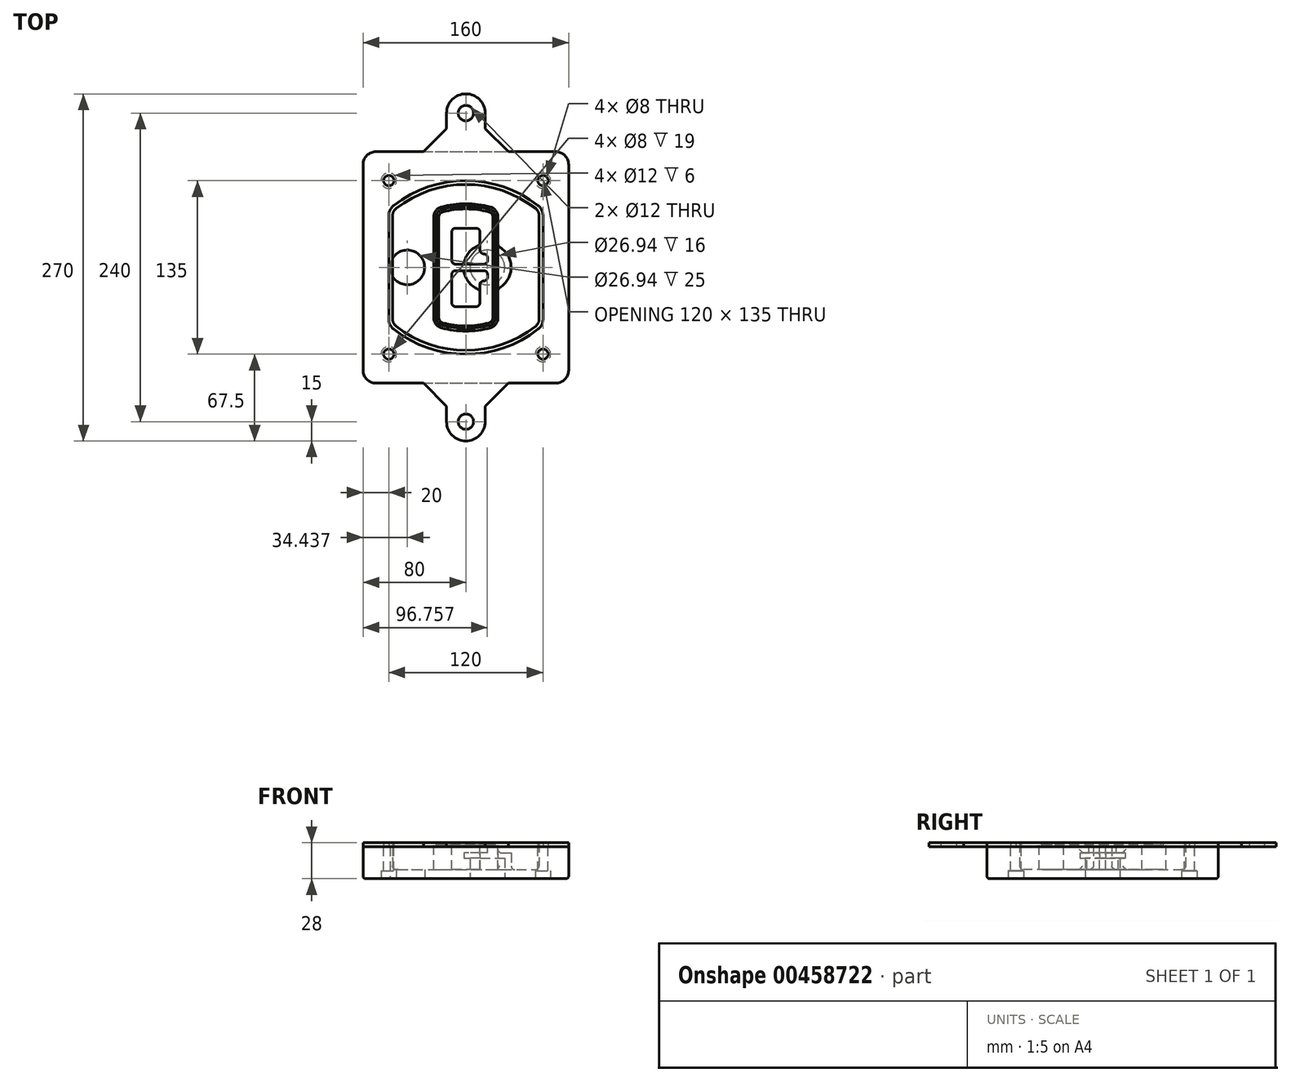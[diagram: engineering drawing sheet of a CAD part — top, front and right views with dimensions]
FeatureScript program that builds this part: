
annotation { "Feature Type Name" : "Feature", "Feature Type Description" : "" }
export const myFeature = defineFeature(function(context is Context, id is Id, definition is map)
    precondition{}
    {
        {
            var Q0;
            Q0=qCreatedBy(makeId("Top.planeOp"),FACE);
            var sketch = newSketch(context, id + "F0", { "sketchPlane" : qUnion([Q0])});
            skPoint(sketch, "E0.rect.middle", {"position": v(0, 0) * mm});
            skLineSegment(sketch, "E1.bottom", {"start": v(-70, -90) * mm, "end": v(70, -90) * mm});
            skLineSegment(sketch, "E1.top", {"start": v(-70, 90) * mm, "end": v(70, 90) * mm});
            skLineSegment(sketch, "E1.left", {"start": v(-80, -80) * mm, "end": v(-80, 80) * mm});
            skLineSegment(sketch, "E1.right", {"start": v(80, -80) * mm, "end": v(80, 80) * mm});
            skLineSegment(sketch, "E2", {"start": v(-80, 90) * mm, "end": v(80, -90) * mm, "construction": true});
            skLineSegment(sketch, "E3", {"start": v(80, 90) * mm, "end": v(-80, -90) * mm, "construction": true});
            skCircle(sketch, "E4", {"center": v(-60, 67.5) * mm, "radius": 4 * mm});
            skCircle(sketch, "E5", {"center": v(60, 67.5) * mm, "radius": 4 * mm});
            skCircle(sketch, "E6", {"center": v(60, -67.5) * mm, "radius": 4 * mm});
            skCircle(sketch, "E7", {"center": v(-60, -67.5) * mm, "radius": 4 * mm});
            skLineSegment(sketch, "E8", {"start": v(-60, 67.5) * mm, "end": v(60, 67.5) * mm, "construction": true});
            skLineSegment(sketch, "E9", {"start": v(60, 67.5) * mm, "end": v(60, -67.5) * mm, "construction": true});
            skLineSegment(sketch, "E10", {"start": v(60, -67.5) * mm, "end": v(-60, -67.5) * mm, "construction": true});
            skLineSegment(sketch, "E11", {"start": v(-60, -67.5) * mm, "end": v(-60, 67.5) * mm, "construction": true});
            skLineSegment(sketch, "E12", {"start": v(-60, 40.3) * mm, "end": v(-60, -40.3) * mm});
            skLineSegment(sketch, "E13", {"start": v(60, 40.3) * mm, "end": v(60, -40.3) * mm});
            skArc(sketch, "E14", {"start": v(56.15, 48.18) * mm, "mid": v(0, 67.5) * mm, "end": v(-56.15, 48.18) * mm});
            skArc(sketch, "E15", {"start": v(-56.15, -48.18) * mm, "mid": v(0, -67.5) * mm, "end": v(56.15, -48.18) * mm});
            skLineSegment(sketch, "E16", {"start": v(-60, 0) * mm, "end": v(60, 0) * mm, "construction": true});
            skPoint(sketch, "E17.visualSharp", {"position": v(-60, -45) * mm});
            skArc(sketch, "E17.filletArc", {"start": v(-60, -40.3) * mm, "mid": v(-58.99, -44.68) * mm, "end": v(-56.15, -48.18) * mm});
            skPoint(sketch, "E18.visualSharp", {"position": v(-60, 45) * mm});
            skArc(sketch, "E18.filletArc", {"start": v(-56.15, 48.18) * mm, "mid": v(-58.99, 44.68) * mm, "end": v(-60, 40.3) * mm});
            skPoint(sketch, "E19.visualSharp", {"position": v(60, 45) * mm});
            skArc(sketch, "E19.filletArc", {"start": v(60, 40.3) * mm, "mid": v(58.99, 44.68) * mm, "end": v(56.15, 48.18) * mm});
            skPoint(sketch, "E20.visualSharp", {"position": v(60, -45) * mm});
            skArc(sketch, "E20.filletArc", {"start": v(56.15, -48.18) * mm, "mid": v(58.99, -44.68) * mm, "end": v(60, -40.3) * mm});
            skPoint(sketch, "E21.visualSharp", {"position": v(-80, 90) * mm});
            skArc(sketch, "E21.filletArc", {"start": v(-70, 90) * mm, "mid": v(-77.07, 87.07) * mm, "end": v(-80, 80) * mm});
            skPoint(sketch, "E22.visualSharp", {"position": v(80, 90) * mm});
            skArc(sketch, "E22.filletArc", {"start": v(80, 80) * mm, "mid": v(77.07, 87.07) * mm, "end": v(70, 90) * mm});
            skPoint(sketch, "E23.visualSharp", {"position": v(80, -90) * mm});
            skArc(sketch, "E23.filletArc", {"start": v(70, -90) * mm, "mid": v(77.07, -87.07) * mm, "end": v(80, -80) * mm});
            skPoint(sketch, "E24.visualSharp", {"position": v(-80, -90) * mm});
            skArc(sketch, "E24.filletArc", {"start": v(-80, -80) * mm, "mid": v(-77.07, -87.07) * mm, "end": v(-70, -90) * mm});
            skArc(sketch, "E25.0", {"start": v(57, 40.3) * mm, "mid": v(56.3, 43.36) * mm, "end": v(54.3, 45.81) * mm});
            skLineSegment(sketch, "E25.1", {"start": v(57, 40.3) * mm, "end": v(57, -40.3) * mm});
            skArc(sketch, "E25.2", {"start": v(54.3, -45.81) * mm, "mid": v(56.3, -43.36) * mm, "end": v(57, -40.3) * mm});
            skArc(sketch, "E25.3", {"start": v(-54.3, -45.81) * mm, "mid": v(0, -64.5) * mm, "end": v(54.3, -45.81) * mm});
            skArc(sketch, "E25.4", {"start": v(-57, -40.3) * mm, "mid": v(-56.3, -43.36) * mm, "end": v(-54.3, -45.81) * mm});
            skArc(sketch, "E25.5", {"start": v(54.3, 45.81) * mm, "mid": v(0, 64.5) * mm, "end": v(-54.3, 45.81) * mm});
            skLineSegment(sketch, "E25.6", {"start": v(-57, 40.3) * mm, "end": v(-57, -40.3) * mm});
            skArc(sketch, "E25.7", {"start": v(-54.3, 45.81) * mm, "mid": v(-56.3, 43.36) * mm, "end": v(-57, 40.3) * mm});
            skArc(sketch, "E26.0", {"start": v(-58.62, 51.33) * mm, "mid": v(-62.58, 46.43) * mm, "end": v(-64, 40.3) * mm});
            skArc(sketch, "E26.1", {"start": v(58.62, 51.33) * mm, "mid": v(0, 71.5) * mm, "end": v(-58.62, 51.33) * mm});
            skArc(sketch, "E26.2", {"start": v(64, 40.3) * mm, "mid": v(62.58, 46.43) * mm, "end": v(58.62, 51.33) * mm});
            skLineSegment(sketch, "E26.3", {"start": v(64, 40.3) * mm, "end": v(64, -40.3) * mm});
            skArc(sketch, "E26.4", {"start": v(58.62, -51.33) * mm, "mid": v(62.58, -46.43) * mm, "end": v(64, -40.3) * mm});
            skLineSegment(sketch, "E26.5", {"start": v(-64, 40.3) * mm, "end": v(-64, -40.3) * mm});
            skArc(sketch, "E26.6", {"start": v(-58.62, -51.33) * mm, "mid": v(0, -71.5) * mm, "end": v(58.62, -51.33) * mm});
            skArc(sketch, "E26.7", {"start": v(-64, -40.3) * mm, "mid": v(-62.58, -46.43) * mm, "end": v(-58.62, -51.33) * mm});
            skSolve(sketch);
        }
        {
            var Q0;
            Q0=makeQuery(id+"F0.imprint","IMPRINT",FACE,{"disambiguationData":[TD([[makeQuery(id+"F0.imprint","IMPRINT",EDGE,{"derivedFrom":sQuery(id+"F0.wireOp",EDGE,"E1.bottom")}),1.0]])]});
            var Q1;
            Q1=makeQuery(id+"F0.imprint","IMPRINT",FACE,{"disambiguationData":[TD([[makeQuery(id+"F0.imprint","IMPRINT",EDGE,{"derivedFrom":sQuery(id+"F0.wireOp",EDGE,"E12")}),1.0]])]});
            var Q2;
            Q2=makeQuery(id+"F0.imprint","IMPRINT",FACE,{"disambiguationData":[TD([[makeQuery(id+"F0.imprint","IMPRINT",EDGE,{"derivedFrom":sQuery(id+"F0.wireOp",EDGE,"E25.0")}),1.0]])]});
            var Q3;
            Q3=makeQuery(id+"F0.imprint","IMPRINT",FACE,{"disambiguationData":[TD([[makeQuery(id+"F0.imprint","IMPRINT",EDGE,{"derivedFrom":sQuery(id+"F0.wireOp",EDGE,"E12")}),-1.0]])]});
            extrude(context, id + "F1", {"entities" : qUnion([Q0, Q1, Q2, Q3]), "oppositeDirection" : true, "depth" : 25 * mm});
        }
        {
            var Q0;
            Q0=makeQuery(id+"F0.imprint","IMPRINT",FACE,{"disambiguationData":[TD([[makeQuery(id+"F0.imprint","IMPRINT",EDGE,{"derivedFrom":sQuery(id+"F0.wireOp",EDGE,"E12")}),1.0]])]});
            extrude(context, id + "F2", {"entities" : qUnion([Q0]), "operationType" : NewBodyOperationType.ADD, "depth" : 3 * mm});
        }
        {
            var Q0;
            Q0=makeQuery(id+"F0.imprint","IMPRINT",FACE,{"disambiguationData":[TD([[makeQuery(id+"F0.imprint","IMPRINT",EDGE,{"derivedFrom":sQuery(id+"F0.wireOp",EDGE,"E25.0")}),1.0]])]});
            extrude(context, id + "F3", {"entities" : qUnion([Q0]), "operationType" : NewBodyOperationType.REMOVE, "oppositeDirection" : true, "depth" : 18 * mm});
        }
        {
            var Q0;
            Q0=makeQuery(id+"F2.opExtrude","CAP_FACE",FACE,{"disambiguationData":[OSD([sQuery(id+"F0.wireOp",EDGE,"E12"),sQuery(id+"F0.wireOp",EDGE,"E13"),sQuery(id+"F0.wireOp",EDGE,"E14"),sQuery(id+"F0.wireOp",EDGE,"E15"),sQuery(id+"F0.wireOp",EDGE,"E17.filletArc"),sQuery(id+"F0.wireOp",EDGE,"E18.filletArc"),sQuery(id+"F0.wireOp",EDGE,"E19.filletArc"),sQuery(id+"F0.wireOp",EDGE,"E20.filletArc"),sQuery(id+"F0.wireOp",EDGE,"E25.0"),sQuery(id+"F0.wireOp",EDGE,"E25.1"),sQuery(id+"F0.wireOp",EDGE,"E25.2"),sQuery(id+"F0.wireOp",EDGE,"E25.3"),sQuery(id+"F0.wireOp",EDGE,"E25.4"),sQuery(id+"F0.wireOp",EDGE,"E25.5"),sQuery(id+"F0.wireOp",EDGE,"E25.6"),sQuery(id+"F0.wireOp",EDGE,"E25.7")])],"isStart":false});
            var sketch = newSketch(context, id + "F4", { "sketchPlane" : qUnion([Q0])});
            skArc(sketch, "E27.0", {"start": v(-19.08, -46.97) * mm, "mid": v(0, -49.5) * mm, "end": v(19.08, -46.97) * mm});
            skArc(sketch, "E28.0", {"start": v(19.08, 46.97) * mm, "mid": v(0, 49.5) * mm, "end": v(-19.08, 46.97) * mm});
            skLineSegment(sketch, "E29", {"start": v(-25, 39.25) * mm, "end": v(-25, -39.25) * mm});
            skLineSegment(sketch, "E30", {"start": v(25, 39.25) * mm, "end": v(25, -39.25) * mm});
            skLineSegment(sketch, "E31", {"start": v(-25, 45.1) * mm, "end": v(25, 45.1) * mm, "construction": true});
            skLineSegment(sketch, "E32", {"start": v(-25, -45.1) * mm, "end": v(25, -45.1) * mm, "construction": true});
            skPoint(sketch, "E33.visualSharp", {"position": v(-25, 45.1) * mm});
            skArc(sketch, "E33.filletArc", {"start": v(-19.08, 46.97) * mm, "mid": v(-23.35, 44.11) * mm, "end": v(-25, 39.25) * mm});
            skPoint(sketch, "E34.visualSharp", {"position": v(25, 45.1) * mm});
            skArc(sketch, "E34.filletArc", {"start": v(25, 39.25) * mm, "mid": v(23.35, 44.11) * mm, "end": v(19.08, 46.97) * mm});
            skPoint(sketch, "E35.visualSharp", {"position": v(25, -45.1) * mm});
            skArc(sketch, "E35.filletArc", {"start": v(19.08, -46.97) * mm, "mid": v(23.35, -44.11) * mm, "end": v(25, -39.25) * mm});
            skPoint(sketch, "E36.visualSharp", {"position": v(-25, -45.1) * mm});
            skArc(sketch, "E36.filletArc", {"start": v(-25, -39.25) * mm, "mid": v(-23.35, -44.11) * mm, "end": v(-19.08, -46.97) * mm});
            skArc(sketch, "E37.0", {"start": v(54.3, 45.81) * mm, "mid": v(0, 64.5) * mm, "end": v(-54.3, 45.81) * mm});
            skArc(sketch, "E37.1", {"start": v(-54.3, 45.81) * mm, "mid": v(-56.3, 43.36) * mm, "end": v(-57, 40.3) * mm});
            skLineSegment(sketch, "E37.2", {"start": v(-57, 40.3) * mm, "end": v(-57, -40.3) * mm});
            skArc(sketch, "E37.3", {"start": v(-57, -40.3) * mm, "mid": v(-56.3, -43.36) * mm, "end": v(-54.3, -45.81) * mm});
            skArc(sketch, "E37.4", {"start": v(-54.3, -45.81) * mm, "mid": v(0, -64.5) * mm, "end": v(54.3, -45.81) * mm});
            skArc(sketch, "E37.5", {"start": v(54.3, -45.81) * mm, "mid": v(56.3, -43.36) * mm, "end": v(57, -40.3) * mm});
            skLineSegment(sketch, "E37.6", {"start": v(57, 40.3) * mm, "end": v(57, -40.3) * mm});
            skArc(sketch, "E37.7", {"start": v(57, 40.3) * mm, "mid": v(56.3, 43.36) * mm, "end": v(54.3, 45.81) * mm});
            skLineSegment(sketch, "E38.0", {"start": v(23, 39.25) * mm, "end": v(23, -39.25) * mm});
            skArc(sketch, "E38.1", {"start": v(18.56, -45.04) * mm, "mid": v(21.76, -42.9) * mm, "end": v(23, -39.25) * mm});
            skArc(sketch, "E38.2", {"start": v(-18.56, -45.04) * mm, "mid": v(0, -47.5) * mm, "end": v(18.56, -45.04) * mm});
            skArc(sketch, "E38.3", {"start": v(-23, -39.25) * mm, "mid": v(-21.76, -42.9) * mm, "end": v(-18.56, -45.04) * mm});
            skLineSegment(sketch, "E38.4", {"start": v(-23, 39.25) * mm, "end": v(-23, -39.25) * mm});
            skArc(sketch, "E38.5", {"start": v(23, 39.25) * mm, "mid": v(21.76, 42.9) * mm, "end": v(18.56, 45.04) * mm});
            skArc(sketch, "E38.6", {"start": v(-18.56, 45.04) * mm, "mid": v(-21.76, 42.9) * mm, "end": v(-23, 39.25) * mm});
            skArc(sketch, "E38.7", {"start": v(18.56, 45.04) * mm, "mid": v(0, 47.5) * mm, "end": v(-18.56, 45.04) * mm});
            skArc(sketch, "E39.0", {"start": v(21, 39.25) * mm, "mid": v(20.18, 41.68) * mm, "end": v(18.04, 43.1) * mm});
            skLineSegment(sketch, "E39.1", {"start": v(21, 39.25) * mm, "end": v(21, -39.25) * mm});
            skArc(sketch, "E39.2", {"start": v(18.04, -43.1) * mm, "mid": v(20.18, -41.68) * mm, "end": v(21, -39.25) * mm});
            skArc(sketch, "E39.3", {"start": v(-18.04, -43.1) * mm, "mid": v(0, -45.5) * mm, "end": v(18.04, -43.1) * mm});
            skArc(sketch, "E39.4", {"start": v(-21, -39.25) * mm, "mid": v(-20.18, -41.68) * mm, "end": v(-18.04, -43.1) * mm});
            skArc(sketch, "E39.5", {"start": v(18.04, 43.1) * mm, "mid": v(0, 45.5) * mm, "end": v(-18.04, 43.1) * mm});
            skLineSegment(sketch, "E39.6", {"start": v(-21, 39.25) * mm, "end": v(-21, -39.25) * mm});
            skArc(sketch, "E39.7", {"start": v(-18.04, 43.1) * mm, "mid": v(-20.18, 41.68) * mm, "end": v(-21, 39.25) * mm});
            skLineSegment(sketch, "E40", {"start": v(-25, 0) * mm, "end": v(25, 0) * mm, "construction": true});
            skLineSegment(sketch, "E41", {"start": v(-11, 5.5) * mm, "end": v(-11, 27.5) * mm});
            skLineSegment(sketch, "E42", {"start": v(-8, 30.5) * mm, "end": v(8, 30.5) * mm});
            skLineSegment(sketch, "E43", {"start": v(11, 27.5) * mm, "end": v(11, 13.5) * mm});
            skLineSegment(sketch, "E44", {"start": v(14, 10.5) * mm, "end": v(14, 10.5) * mm});
            skLineSegment(sketch, "E45", {"start": v(17, 7.5) * mm, "end": v(17, 5.5) * mm});
            skLineSegment(sketch, "E46", {"start": v(14, 2.5) * mm, "end": v(-8, 2.5) * mm});
            skPoint(sketch, "E47.visualSharp", {"position": v(-11, 30.5) * mm});
            skArc(sketch, "E47.filletArc", {"start": v(-8, 30.5) * mm, "mid": v(-10.12, 29.62) * mm, "end": v(-11, 27.5) * mm});
            skPoint(sketch, "E48.visualSharp", {"position": v(11, 30.5) * mm});
            skArc(sketch, "E48.filletArc", {"start": v(11, 27.5) * mm, "mid": v(10.12, 29.62) * mm, "end": v(8, 30.5) * mm});
            skPoint(sketch, "E49.visualSharp", {"position": v(11, 10.5) * mm});
            skArc(sketch, "E49.filletArc", {"start": v(11, 13.5) * mm, "mid": v(11.88, 11.38) * mm, "end": v(14, 10.5) * mm});
            skPoint(sketch, "E50.visualSharp", {"position": v(17, 10.5) * mm});
            skArc(sketch, "E50.filletArc", {"start": v(17, 7.5) * mm, "mid": v(16.12, 9.62) * mm, "end": v(14, 10.5) * mm});
            skPoint(sketch, "E51.visualSharp", {"position": v(17, 2.5) * mm});
            skArc(sketch, "E51.filletArc", {"start": v(14, 2.5) * mm, "mid": v(16.12, 3.38) * mm, "end": v(17, 5.5) * mm});
            skPoint(sketch, "E52.visualSharp", {"position": v(-11, 2.5) * mm});
            skArc(sketch, "E52.filletArc", {"start": v(-11, 5.5) * mm, "mid": v(-10.12, 3.38) * mm, "end": v(-8, 2.5) * mm});
            skLineSegment(sketch, "E53.0.MirrorCS", {"start": v(14, -2.5) * mm, "end": v(-8, -2.5) * mm});
            skArc(sketch, "E54.0.MirrorCS", {"start": v(-11, -5.5) * mm, "mid": v(-10.12, -3.38) * mm, "end": v(-8, -2.5) * mm});
            skLineSegment(sketch, "E55.0.MirrorCS", {"start": v(-11, -5.5) * mm, "end": v(-11, -27.5) * mm});
            skArc(sketch, "E56.0.MirrorCS", {"start": v(-8, -30.5) * mm, "mid": v(-10.12, -29.62) * mm, "end": v(-11, -27.5) * mm});
            skLineSegment(sketch, "E57.0.MirrorCS", {"start": v(-8, -30.5) * mm, "end": v(8, -30.5) * mm});
            skArc(sketch, "E58.0.MirrorCS", {"start": v(11, -27.5) * mm, "mid": v(10.12, -29.62) * mm, "end": v(8, -30.5) * mm});
            skLineSegment(sketch, "E59.0.MirrorCS", {"start": v(11, -27.5) * mm, "end": v(11, -13.5) * mm});
            skArc(sketch, "E60.0.MirrorCS", {"start": v(11, -13.5) * mm, "mid": v(11.88, -11.38) * mm, "end": v(14, -10.5) * mm});
            skArc(sketch, "E61.0.MirrorCS", {"start": v(17, -7.5) * mm, "mid": v(16.12, -9.62) * mm, "end": v(14, -10.5) * mm});
            skLineSegment(sketch, "E62.0.MirrorCS", {"start": v(17, -7.5) * mm, "end": v(17, -5.5) * mm});
            skArc(sketch, "E63.0.MirrorCS", {"start": v(14, -2.5) * mm, "mid": v(16.12, -3.38) * mm, "end": v(17, -5.5) * mm});
            skSolve(sketch);
        }
        {
            var Q0;
            Q0=makeQuery(id+"F4.imprint","IMPRINT",FACE,{"disambiguationData":[TD([[makeQuery(id+"F4.imprint","IMPRINT",EDGE,{"derivedFrom":sQuery(id+"F4.wireOp",EDGE,"E27.0")}),1.0]])]});
            var Q1;
            Q1=makeQuery(id+"F4.imprint","IMPRINT",FACE,{"disambiguationData":[TD([[makeQuery(id+"F4.imprint","IMPRINT",EDGE,{"derivedFrom":sQuery(id+"F4.wireOp",EDGE,"E38.0")}),-1.0]])]});
            var Q2;
            Q2=makeQuery(id+"F4.imprint","IMPRINT",FACE,{"disambiguationData":[TD([[makeQuery(id+"F4.imprint","IMPRINT",EDGE,{"derivedFrom":sQuery(id+"F4.wireOp",EDGE,"E39.0")}),1.0]])]});
            extrude(context, id + "F5", {"entities" : qUnion([Q0, Q1, Q2]), "operationType" : NewBodyOperationType.ADD, "endBound" : BoundingType.UP_TO_NEXT, "oppositeDirection" : true, "depth" : 25 * mm});
        }
        {
            var Q0;
            Q0=makeQuery(id+"F4.imprint","IMPRINT",FACE,{"disambiguationData":[TD([[makeQuery(id+"F4.imprint","IMPRINT",EDGE,{"derivedFrom":sQuery(id+"F4.wireOp",EDGE,"E38.0")}),-1.0]])]});
            extrude(context, id + "F6", {"entities" : qUnion([Q0]), "operationType" : NewBodyOperationType.REMOVE, "oppositeDirection" : true, "depth" : 2 * mm});
        }
        {
            var Q0;
            Q0=makeQuery(id+"F1.opExtrude","CAP_FACE",FACE,{"disambiguationData":[OSD([sQuery(id+"F0.wireOp",EDGE,"E1.bottom"),sQuery(id+"F0.wireOp",EDGE,"E1.top"),sQuery(id+"F0.wireOp",EDGE,"E1.left"),sQuery(id+"F0.wireOp",EDGE,"E1.right"),sQuery(id+"F0.wireOp",EDGE,"E4"),sQuery(id+"F0.wireOp",EDGE,"E5"),sQuery(id+"F0.wireOp",EDGE,"E6"),sQuery(id+"F0.wireOp",EDGE,"E7"),sQuery(id+"F0.wireOp",EDGE,"E21.filletArc"),sQuery(id+"F0.wireOp",EDGE,"E22.filletArc"),sQuery(id+"F0.wireOp",EDGE,"E23.filletArc"),sQuery(id+"F0.wireOp",EDGE,"E24.filletArc")])],"isStart":false});
            var sketch = newSketch(context, id + "F7", { "sketchPlane" : qUnion([Q0])});
            skCircle(sketch, "E64", {"center": v(16.76, 0) * mm, "radius": 13.47 * mm});
            skCircle(sketch, "E65", {"center": v(-45.56, 0) * mm, "radius": 13.47 * mm});
            skLineSegment(sketch, "E66", {"start": v(80, 0) * mm, "end": v(-80, 0) * mm});
            skCircle(sketch, "E67", {"center": v(16.76, 0) * mm, "radius": 18.47 * mm});
            skCircle(sketch, "E68", {"center": v(60, -67.5) * mm, "radius": 6 * mm});
            skCircle(sketch, "E69", {"center": v(-60, -67.5) * mm, "radius": 6 * mm});
            skCircle(sketch, "E70", {"center": v(-60, 67.5) * mm, "radius": 6 * mm});
            skCircle(sketch, "E71", {"center": v(60, 67.5) * mm, "radius": 6 * mm});
            skSolve(sketch);
        }
        {
            var Q0;
            {var subQ1=sQuery(id+"F7.wireOp",EDGE,"E66");var subQ4=sQuery(id+"F7.wireOp",EDGE,"E64");var subQ6=makeQuery(id+"F7.imprint","INTERSECT",VERTEX,{"disambiguationData":[OD(0.0)],"derivedFrom":[subQ4,subQ1]});Q0=makeQuery(id+"F7.imprint","IMPRINT",FACE,{"disambiguationData":[TD([[makeQuery(id+"F7.imprint","IMPRINT",EDGE,{"disambiguationData":[TD([[subQ6,-1.0]])],"derivedFrom":subQ4}),-1.0]])]});}
            var Q1;
            {var subQ0=sQuery(id+"F7.wireOp",EDGE,"E66");var subQ1=sQuery(id+"F7.wireOp",EDGE,"E64");var subQ3=makeQuery(id+"F7.imprint","INTERSECT",VERTEX,{"disambiguationData":[OD(0.0)],"derivedFrom":[subQ1,subQ0]});Q1=makeQuery(id+"F7.imprint","IMPRINT",FACE,{"disambiguationData":[TD([[makeQuery(id+"F7.imprint","IMPRINT",EDGE,{"disambiguationData":[TD([[subQ3,-1.0]])],"derivedFrom":subQ1}),1.0]])]});}
            var Q2;
            {var subQ0=sQuery(id+"F7.wireOp",EDGE,"E66");var subQ1=sQuery(id+"F7.wireOp",EDGE,"E64");var subQ3=makeQuery(id+"F7.imprint","INTERSECT",VERTEX,{"disambiguationData":[OD(0.0)],"derivedFrom":[subQ1,subQ0]});Q2=makeQuery(id+"F7.imprint","IMPRINT",FACE,{"disambiguationData":[TD([[makeQuery(id+"F7.imprint","IMPRINT",EDGE,{"disambiguationData":[TD([[subQ3,1.0]])],"derivedFrom":subQ1}),1.0]])]});}
            var Q3;
            {var subQ1=sQuery(id+"F7.wireOp",EDGE,"E66");var subQ4=sQuery(id+"F7.wireOp",EDGE,"E64");var subQ6=makeQuery(id+"F7.imprint","INTERSECT",VERTEX,{"disambiguationData":[OD(0.0)],"derivedFrom":[subQ4,subQ1]});Q3=makeQuery(id+"F7.imprint","IMPRINT",FACE,{"disambiguationData":[TD([[makeQuery(id+"F7.imprint","IMPRINT",EDGE,{"disambiguationData":[TD([[subQ6,1.0]])],"derivedFrom":subQ4}),-1.0]])]});}
            extrude(context, id + "F8", {"entities" : qUnion([Q0, Q1, Q2, Q3]), "operationType" : NewBodyOperationType.ADD, "oppositeDirection" : true, "depth" : 20 * mm});
        }
        {
            var Q0;
            {var subQ0=sQuery(id+"F7.wireOp",EDGE,"E66");var subQ1=sQuery(id+"F7.wireOp",EDGE,"E64");var subQ3=makeQuery(id+"F7.imprint","INTERSECT",VERTEX,{"disambiguationData":[OD(0.0)],"derivedFrom":[subQ1,subQ0]});Q0=makeQuery(id+"F7.imprint","IMPRINT",FACE,{"disambiguationData":[TD([[makeQuery(id+"F7.imprint","IMPRINT",EDGE,{"disambiguationData":[TD([[subQ3,-1.0]])],"derivedFrom":subQ1}),1.0]])]});}
            var Q1;
            {var subQ0=sQuery(id+"F7.wireOp",EDGE,"E66");var subQ1=sQuery(id+"F7.wireOp",EDGE,"E64");var subQ3=makeQuery(id+"F7.imprint","INTERSECT",VERTEX,{"disambiguationData":[OD(0.0)],"derivedFrom":[subQ1,subQ0]});Q1=makeQuery(id+"F7.imprint","IMPRINT",FACE,{"disambiguationData":[TD([[makeQuery(id+"F7.imprint","IMPRINT",EDGE,{"disambiguationData":[TD([[subQ3,1.0]])],"derivedFrom":subQ1}),1.0]])]});}
            extrude(context, id + "F9", {"entities" : qUnion([Q0, Q1]), "operationType" : NewBodyOperationType.REMOVE, "oppositeDirection" : true, "depth" : 16 * mm});
        }
        {
            var Q0;
            {var subQ0=sQuery(id+"F7.wireOp",EDGE,"E66");var subQ1=sQuery(id+"F7.wireOp",EDGE,"E65");var subQ3=makeQuery(id+"F7.imprint","INTERSECT",VERTEX,{"disambiguationData":[OD(0.0)],"derivedFrom":[subQ1,subQ0]});Q0=makeQuery(id+"F7.imprint","IMPRINT",FACE,{"disambiguationData":[TD([[makeQuery(id+"F7.imprint","IMPRINT",EDGE,{"disambiguationData":[TD([[subQ3,-1.0]])],"derivedFrom":subQ1}),1.0]])]});}
            var Q1;
            {var subQ0=sQuery(id+"F7.wireOp",EDGE,"E66");var subQ1=sQuery(id+"F7.wireOp",EDGE,"E65");var subQ3=makeQuery(id+"F7.imprint","INTERSECT",VERTEX,{"disambiguationData":[OD(0.0)],"derivedFrom":[subQ1,subQ0]});Q1=makeQuery(id+"F7.imprint","IMPRINT",FACE,{"disambiguationData":[TD([[makeQuery(id+"F7.imprint","IMPRINT",EDGE,{"disambiguationData":[TD([[subQ3,1.0]])],"derivedFrom":subQ1}),1.0]])]});}
            extrude(context, id + "F10", {"entities" : qUnion([Q0, Q1]), "operationType" : NewBodyOperationType.REMOVE, "oppositeDirection" : true, "depth" : 25 * mm});
        }
        {
            var Q0;
            Q0=makeQuery(id+"F7.imprint","IMPRINT",FACE,{"disambiguationData":[TD([[makeQuery(id+"F7.imprint","IMPRINT",EDGE,{"derivedFrom":sQuery(id+"F7.wireOp",EDGE,"E68")}),1.0]])]});
            var Q1;
            Q1=makeQuery(id+"F7.imprint","IMPRINT",FACE,{"disambiguationData":[TD([[makeQuery(id+"F7.imprint","IMPRINT",EDGE,{"derivedFrom":makeQuery(id+"F1.opExtrude","CAP_EDGE",EDGE,{"disambiguationData":[OSD([sQuery(id+"F0.wireOp",EDGE,"E5")])],"isStart":false})}),-1.0]])]});
            var Q2;
            Q2=makeQuery(id+"F7.imprint","IMPRINT",FACE,{"disambiguationData":[TD([[makeQuery(id+"F7.imprint","IMPRINT",EDGE,{"derivedFrom":sQuery(id+"F7.wireOp",EDGE,"E69")}),1.0]])]});
            var Q3;
            Q3=makeQuery(id+"F7.imprint","IMPRINT",FACE,{"disambiguationData":[TD([[makeQuery(id+"F7.imprint","IMPRINT",EDGE,{"derivedFrom":makeQuery(id+"F1.opExtrude","CAP_EDGE",EDGE,{"disambiguationData":[OSD([sQuery(id+"F0.wireOp",EDGE,"E4")])],"isStart":false})}),-1.0]])]});
            var Q4;
            Q4=makeQuery(id+"F7.imprint","IMPRINT",FACE,{"disambiguationData":[TD([[makeQuery(id+"F7.imprint","IMPRINT",EDGE,{"derivedFrom":sQuery(id+"F7.wireOp",EDGE,"E70")}),1.0]])]});
            var Q5;
            Q5=makeQuery(id+"F7.imprint","IMPRINT",FACE,{"disambiguationData":[TD([[makeQuery(id+"F7.imprint","IMPRINT",EDGE,{"derivedFrom":makeQuery(id+"F1.opExtrude","CAP_EDGE",EDGE,{"disambiguationData":[OSD([sQuery(id+"F0.wireOp",EDGE,"E7")])],"isStart":false})}),-1.0]])]});
            var Q6;
            Q6=makeQuery(id+"F7.imprint","IMPRINT",FACE,{"disambiguationData":[TD([[makeQuery(id+"F7.imprint","IMPRINT",EDGE,{"derivedFrom":sQuery(id+"F7.wireOp",EDGE,"E71")}),1.0]])]});
            var Q7;
            Q7=makeQuery(id+"F7.imprint","IMPRINT",FACE,{"disambiguationData":[TD([[makeQuery(id+"F7.imprint","IMPRINT",EDGE,{"derivedFrom":makeQuery(id+"F1.opExtrude","CAP_EDGE",EDGE,{"disambiguationData":[OSD([sQuery(id+"F0.wireOp",EDGE,"E6")])],"isStart":false})}),-1.0]])]});
            extrude(context, id + "F11", {"entities" : qUnion([Q0, Q1, Q2, Q3, Q4, Q5, Q6, Q7]), "operationType" : NewBodyOperationType.REMOVE, "oppositeDirection" : true, "depth" : 6 * mm});
        }
        {
            var Q0;
            Q0=makeQuery(id+"F9.boolean.opBoolean","COPY",FACE,{"derivedFrom":makeQuery(id+"F9.opExtrude","CAP_FACE",FACE,{"disambiguationData":[OSD([sQuery(id+"F7.wireOp",EDGE,"E64")])],"isStart":false})});
            var sketch = newSketch(context, id + "F12", { "sketchPlane" : qUnion([Q0])});
            skArc(sketch, "E72.0", {"start": v(11, 17.55) * mm, "mid": v(2.57, 11.82) * mm, "end": v(-1.54, 2.5) * mm});
            skArc(sketch, "E72.1", {"start": v(-1.54, -2.5) * mm, "mid": v(2.57, -11.82) * mm, "end": v(11, -17.55) * mm});
            skLineSegment(sketch, "E73", {"start": v(-1.54, -2.5) * mm, "end": v(14, -2.5) * mm});
            skLineSegment(sketch, "E74.0", {"start": v(14, 2.5) * mm, "end": v(-1.54, 2.5) * mm});
            skArc(sketch, "E74.1", {"start": v(14, 2.5) * mm, "mid": v(16.12, 3.38) * mm, "end": v(17, 5.5) * mm});
            skLineSegment(sketch, "E74.2", {"start": v(17, 7.5) * mm, "end": v(17, 5.5) * mm});
            skArc(sketch, "E74.3", {"start": v(17, 7.5) * mm, "mid": v(16.12, 9.62) * mm, "end": v(14, 10.5) * mm});
            skArc(sketch, "E74.4", {"start": v(11, 13.5) * mm, "mid": v(11.88, 11.38) * mm, "end": v(14, 10.5) * mm});
            skLineSegment(sketch, "E74.5", {"start": v(11, 17.55) * mm, "end": v(11, 13.5) * mm});
            skLineSegment(sketch, "E74.7", {"start": v(14, -2.5) * mm, "end": v(-1.54, -2.5) * mm});
            skArc(sketch, "E74.8", {"start": v(14, -2.5) * mm, "mid": v(16.12, -3.38) * mm, "end": v(17, -5.5) * mm});
            skLineSegment(sketch, "E74.9", {"start": v(17, -7.5) * mm, "end": v(17, -5.5) * mm});
            skArc(sketch, "E74.10", {"start": v(17, -7.5) * mm, "mid": v(16.12, -9.62) * mm, "end": v(14, -10.5) * mm});
            skArc(sketch, "E74.11", {"start": v(11, -13.5) * mm, "mid": v(11.88, -11.38) * mm, "end": v(14, -10.5) * mm});
            skLineSegment(sketch, "E74.12", {"start": v(11, -17.55) * mm, "end": v(11, -13.5) * mm});
            skPoint(sketch, "E75.orphan", {"position": v(11, -27.5) * mm});
            skPoint(sketch, "E76.orphan", {"position": v(-8, -2.5) * mm});
            skPoint(sketch, "E77.orphan", {"position": v(-8, 2.5) * mm});
            skPoint(sketch, "E78.orphan", {"position": v(11, 27.5) * mm});
            skSolve(sketch);
        }
        {
            var Q0;
            {var subQ7=sQuery(id+"F12.wireOp",EDGE,"E72.0");var subQ14=sQuery(id+"F12.wireOp",EDGE,"E72.1");var subQ16=sQuery(id+"F12.wireOp",EDGE,"E74.1");var subQ18=sQuery(id+"F12.wireOp",EDGE,"E74.8");Q0=qUnion([makeQuery(id+"F12.imprint","IMPRINT",FACE,{"disambiguationData":[TD([[makeQuery(id+"F12.imprint","IMPRINT",EDGE,{"derivedFrom":subQ7}),1.0]])]}),makeQuery(id+"F12.imprint","IMPRINT",FACE,{"disambiguationData":[TD([[makeQuery(id+"F12.imprint","IMPRINT",EDGE,{"derivedFrom":subQ14}),1.0]])]}),makeQuery(id+"F12.imprint","IMPRINT",FACE,{"disambiguationData":[TD([[makeQuery(id+"F12.imprint","IMPRINT",EDGE,{"derivedFrom":subQ16}),1.0]])]}),makeQuery(id+"F12.imprint","IMPRINT",FACE,{"disambiguationData":[TD([[makeQuery(id+"F12.imprint","IMPRINT",EDGE,{"derivedFrom":subQ18}),-1.0]])]})]);}
            var Q1;
            Q1=makeQuery(id+"F5.boolean.opBoolean","SPLIT",FACE,{"disambiguationData":[TD([makeQuery(id+"F5.opExtrude","SWEPT_FACE",FACE,{"disambiguationData":[OSD([sQuery(id+"F4.wireOp",EDGE,"E41")])]})])],"derivedFrom":makeQuery(id+"F3.boolean.opBoolean","COPY",FACE,{"derivedFrom":makeQuery(id+"F3.opExtrude","CAP_FACE",FACE,{"disambiguationData":[OSD([sQuery(id+"F0.wireOp",EDGE,"E25.0"),sQuery(id+"F0.wireOp",EDGE,"E25.1"),sQuery(id+"F0.wireOp",EDGE,"E25.2"),sQuery(id+"F0.wireOp",EDGE,"E25.3"),sQuery(id+"F0.wireOp",EDGE,"E25.4"),sQuery(id+"F0.wireOp",EDGE,"E25.5"),sQuery(id+"F0.wireOp",EDGE,"E25.6"),sQuery(id+"F0.wireOp",EDGE,"E25.7")])],"isStart":false})})});
            extrude(context, id + "F13", {"entities" : qUnion([Q0]), "operationType" : NewBodyOperationType.REMOVE, "endBound" : BoundingType.UP_TO_SURFACE, "endBoundEntityFace" : qUnion([Q1]), "depth" : 25 * mm});
        }
        {
            var Q0;
            Q0=makeQuery(id+"F3.boolean.opBoolean","COPY",EDGE,{"derivedFrom":makeQuery(id+"F3.opExtrude","CAP_EDGE",EDGE,{"disambiguationData":[OSD([sQuery(id+"F0.wireOp",EDGE,"E25.6")])],"isStart":false})});
            var Q1;
            Q1=makeQuery(id+"F8.boolean.opBoolean","INTERSECT",EDGE,{"derivedFrom":[makeQuery(id+"F5.opExtrude","SWEPT_FACE",FACE,{"disambiguationData":[OSD([sQuery(id+"F4.wireOp",EDGE,"E30")])]}),makeQuery(id+"F8.opExtrude","CAP_FACE",FACE,{"disambiguationData":[OSD([sQuery(id+"F7.wireOp",EDGE,"E67")])],"isStart":false})]});
            var Q2;
            Q2=makeQuery(id+"F8.boolean.opBoolean","INTERSECT",EDGE,{"disambiguationData":[OD(1.0)],"derivedFrom":[makeQuery(id+"F5.opExtrude","SWEPT_FACE",FACE,{"disambiguationData":[OSD([sQuery(id+"F4.wireOp",EDGE,"E30")])]}),makeQuery(id+"F8.opExtrude","SWEPT_FACE",FACE,{"disambiguationData":[OSD([sQuery(id+"F7.wireOp",EDGE,"E67")])]})]});
            var Q3;
            {var subQ0=makeQuery(id+"F3.boolean.opBoolean","COPY",FACE,{"derivedFrom":makeQuery(id+"F3.opExtrude","CAP_FACE",FACE,{"disambiguationData":[OSD([sQuery(id+"F0.wireOp",EDGE,"E25.0"),sQuery(id+"F0.wireOp",EDGE,"E25.1"),sQuery(id+"F0.wireOp",EDGE,"E25.2"),sQuery(id+"F0.wireOp",EDGE,"E25.3"),sQuery(id+"F0.wireOp",EDGE,"E25.4"),sQuery(id+"F0.wireOp",EDGE,"E25.5"),sQuery(id+"F0.wireOp",EDGE,"E25.6"),sQuery(id+"F0.wireOp",EDGE,"E25.7")])],"isStart":false})});var subQ1=sQuery(id+"F4.wireOp",EDGE,"E30");Q3=makeQuery(id+"F8.boolean.opBoolean","SPLIT",EDGE,{"disambiguationData":[TD([makeQuery(id+"F5.opExtrude","SWEPT_FACE",FACE,{"disambiguationData":[OSD([sQuery(id+"F4.wireOp",EDGE,"E35.filletArc")])]})])],"derivedFrom":makeQuery(id+"F5.opExtrude","TWEAK_EDGE",EDGE,{"derivedFrom":[subQ0,makeQuery(id+"F4.imprint","IMPRINT",EDGE,{"derivedFrom":subQ1})]})});}
            var Q4;
            {var subQ0=sQuery(id+"F0.wireOp",EDGE,"E25.0");var subQ1=sQuery(id+"F0.wireOp",EDGE,"E25.1");var subQ2=sQuery(id+"F0.wireOp",EDGE,"E25.2");var subQ3=sQuery(id+"F0.wireOp",EDGE,"E25.3");var subQ4=sQuery(id+"F0.wireOp",EDGE,"E25.4");var subQ5=sQuery(id+"F0.wireOp",EDGE,"E25.5");var subQ6=sQuery(id+"F0.wireOp",EDGE,"E25.6");var subQ7=sQuery(id+"F0.wireOp",EDGE,"E25.7");Q4=makeQuery(id+"F8.boolean.opBoolean","INTERSECT",EDGE,{"derivedFrom":[makeQuery(id+"F5.boolean.opBoolean","SPLIT",FACE,{"disambiguationData":[TD([makeQuery(id+"F2.opExtrude","SWEPT_FACE",FACE,{"disambiguationData":[OSD([subQ0])]})])],"derivedFrom":makeQuery(id+"F3.boolean.opBoolean","COPY",FACE,{"derivedFrom":makeQuery(id+"F3.opExtrude","CAP_FACE",FACE,{"disambiguationData":[OSD([subQ0,subQ1,subQ2,subQ3,subQ4,subQ5,subQ6,subQ7])],"isStart":false})})}),makeQuery(id+"F8.opExtrude","SWEPT_FACE",FACE,{"disambiguationData":[OSD([sQuery(id+"F7.wireOp",EDGE,"E67")])]})]});}
            var Q5;
            Q5=makeQuery(id+"F8.boolean.opBoolean","INTERSECT",EDGE,{"disambiguationData":[OD(0.0)],"derivedFrom":[makeQuery(id+"F5.opExtrude","SWEPT_FACE",FACE,{"disambiguationData":[OSD([sQuery(id+"F4.wireOp",EDGE,"E30")])]}),makeQuery(id+"F8.opExtrude","SWEPT_FACE",FACE,{"disambiguationData":[OSD([sQuery(id+"F7.wireOp",EDGE,"E67")])]})]});
            fillet(context, id + "F14", {"entities" : qUnion([Q0, Q1, Q2, Q3, Q4, Q5]), "radius" : 3 * mm, "tangentPropagation" : true, "allowEdgeOverflow" : false});
        }
        {
            var Q0;
            Q0=makeQuery(id+"F1.opExtrude","CAP_EDGE",EDGE,{"disambiguationData":[OSD([sQuery(id+"F0.wireOp",EDGE,"E1.bottom")])],"isStart":false});
            fillet(context, id + "F15", {"entities" : qUnion([Q0]), "radius" : 2 * mm, "tangentPropagation" : true, "allowEdgeOverflow" : false});
        }
        {
            var Q0;
            {var subQ0=sQuery(id+"F0.wireOp",EDGE,"E21.filletArc");var subQ1=sQuery(id+"F0.wireOp",EDGE,"E7");var subQ2=sQuery(id+"F0.wireOp",EDGE,"E6");var subQ3=sQuery(id+"F0.wireOp",EDGE,"E5");var subQ4=sQuery(id+"F0.wireOp",EDGE,"E4");var subQ5=sQuery(id+"F0.wireOp",EDGE,"E22.filletArc");var subQ6=sQuery(id+"F0.wireOp",EDGE,"E1.bottom");var subQ7=sQuery(id+"F0.wireOp",EDGE,"E1.right");var subQ8=sQuery(id+"F0.wireOp",EDGE,"E1.top");var subQ9=sQuery(id+"F0.wireOp",EDGE,"E1.left");var subQ10=sQuery(id+"F0.wireOp",EDGE,"E23.filletArc");var subQ11=sQuery(id+"F0.wireOp",EDGE,"E24.filletArc");Q0=makeQuery(id+"F2.boolean.opBoolean","SPLIT",FACE,{"disambiguationData":[TD([makeQuery(id+"F1.opExtrude","SWEPT_FACE",FACE,{"disambiguationData":[OSD([subQ6])]})])],"derivedFrom":makeQuery(id+"F1.opExtrude","CAP_FACE",FACE,{"disambiguationData":[OSD([subQ6,subQ8,subQ9,subQ7,subQ4,subQ3,subQ2,subQ1,subQ0,subQ5,subQ10,subQ11])],"isStart":true})});}
            var sketch = newSketch(context, id + "F16", { "sketchPlane" : qUnion([Q0])});
            skLineSegment(sketch, "E79.0", {"start": v(-70, 90) * mm, "end": v(70, 90) * mm});
            skArc(sketch, "E79.1", {"start": v(-70, 90) * mm, "mid": v(-77.07, 87.07) * mm, "end": v(-80, 80) * mm});
            skLineSegment(sketch, "E79.2", {"start": v(-80, -80) * mm, "end": v(-80, 80) * mm});
            skArc(sketch, "E79.3", {"start": v(-80, -80) * mm, "mid": v(-77.07, -87.07) * mm, "end": v(-70, -90) * mm});
            skLineSegment(sketch, "E79.4", {"start": v(-70, -90) * mm, "end": v(70, -90) * mm});
            skArc(sketch, "E79.5", {"start": v(70, -90) * mm, "mid": v(77.07, -87.07) * mm, "end": v(80, -80) * mm});
            skLineSegment(sketch, "E79.6", {"start": v(80, -80) * mm, "end": v(80, 80) * mm});
            skArc(sketch, "E79.7", {"start": v(80, 80) * mm, "mid": v(77.07, 87.07) * mm, "end": v(70, 90) * mm});
            skCircle(sketch, "E79.8", {"center": v(-60, 67.5) * mm, "radius": 4 * mm});
            skCircle(sketch, "E79.9", {"center": v(60, 67.5) * mm, "radius": 4 * mm});
            skCircle(sketch, "E79.10", {"center": v(60, -67.5) * mm, "radius": 4 * mm});
            skCircle(sketch, "E79.11", {"center": v(-60, -67.5) * mm, "radius": 4 * mm});
            skLineSegment(sketch, "E80", {"start": v(-80, 0) * mm, "end": v(80, 0) * mm, "construction": true});
            skLineSegment(sketch, "E81", {"start": v(0, 90) * mm, "end": v(0, 120) * mm, "construction": true});
            skLineSegment(sketch, "E82", {"start": v(-33, 90) * mm, "end": v(-15, 108) * mm});
            skLineSegment(sketch, "E83", {"start": v(33, 90) * mm, "end": v(15, 108) * mm});
            skCircle(sketch, "E84", {"center": v(0, 120) * mm, "radius": 6 * mm});
            skArc(sketch, "E85", {"start": v(-15, 120) * mm, "mid": v(0, 135) * mm, "end": v(15, 120) * mm});
            skLineSegment(sketch, "E86", {"start": v(-15, 108) * mm, "end": v(-15, 120) * mm});
            skLineSegment(sketch, "E87", {"start": v(15, 108) * mm, "end": v(15, 120) * mm});
            skLineSegment(sketch, "E88.MirrorCS", {"start": v(-15, -108) * mm, "end": v(-15, -120) * mm});
            skLineSegment(sketch, "E89.MirrorCS", {"start": v(-33, -90) * mm, "end": v(-15, -108) * mm});
            skLineSegment(sketch, "E90.MirrorCS", {"start": v(33, -90) * mm, "end": v(15, -108) * mm});
            skLineSegment(sketch, "E91.MirrorCS", {"start": v(15, -108) * mm, "end": v(15, -120) * mm});
            skArc(sketch, "E92.MirrorCS", {"start": v(-15, -120) * mm, "mid": v(0, -135) * mm, "end": v(15, -120) * mm});
            skCircle(sketch, "E93.MirrorC", {"center": v(0, -120) * mm, "radius": 6 * mm});
            skSolve(sketch);
        }
        {
            var Q0;
            Q0=makeQuery(id+"F16.imprint","IMPRINT",FACE,{"disambiguationData":[TD([[makeQuery(id+"F16.imprint","IMPRINT",EDGE,{"derivedFrom":sQuery(id+"F16.wireOp",EDGE,"LAyB9Eon-A8TJ-eU6J-R6AS-ih3Y1rFErONo")}),-1.0]])]});
            var Q1;
            {var subQ1=sQuery(id+"F16.wireOp",EDGE,"E79.1");Q1=makeQuery(id+"F16.imprint","IMPRINT",FACE,{"disambiguationData":[TD([[makeQuery(id+"F16.imprint","IMPRINT",EDGE,{"derivedFrom":subQ1}),1.0]])]});}
            var Q2;
            Q2=makeQuery(id+"F16.imprint","IMPRINT",FACE,{"disambiguationData":[TD([[makeQuery(id+"F16.imprint","IMPRINT",EDGE,{"derivedFrom":sQuery(id+"F16.wireOp",EDGE,"LAyB9Eon-A8TJ-eU6J-R6AS-ih3Y1rFErONo")}),1.0]])]});
            var Q3;
            {var subQ1=sQuery(id+"F16.wireOp",EDGE,"7e09a80c-e641-4784-bf9e-b96955cbc9d70.MirrorCS");Q3=makeQuery(id+"F16.imprint","IMPRINT",FACE,{"disambiguationData":[TD([[makeQuery(id+"F16.imprint","IMPRINT",EDGE,{"derivedFrom":subQ1}),1.0]])]});}
            var Q4;
            {var subQ1=sQuery(id+"F16.wireOp",EDGE,"E82");Q4=makeQuery(id+"F16.imprint","IMPRINT",FACE,{"disambiguationData":[TD([[makeQuery(id+"F16.imprint","IMPRINT",EDGE,{"derivedFrom":subQ1}),-1.0]])]});}
            var Q5;
            {var subQ1=sQuery(id+"F16.wireOp",EDGE,"E89.MirrorCS");Q5=makeQuery(id+"F16.imprint","IMPRINT",FACE,{"disambiguationData":[TD([[makeQuery(id+"F16.imprint","IMPRINT",EDGE,{"derivedFrom":subQ1}),1.0]])]});}
            var Q6;
            Q6=makeQuery(id+"F2.opExtrude","CAP_FACE",FACE,{"disambiguationData":[OSD([sQuery(id+"F0.wireOp",EDGE,"E12"),sQuery(id+"F0.wireOp",EDGE,"E13"),sQuery(id+"F0.wireOp",EDGE,"E14"),sQuery(id+"F0.wireOp",EDGE,"E15"),sQuery(id+"F0.wireOp",EDGE,"E17.filletArc"),sQuery(id+"F0.wireOp",EDGE,"E18.filletArc"),sQuery(id+"F0.wireOp",EDGE,"E19.filletArc"),sQuery(id+"F0.wireOp",EDGE,"E20.filletArc"),sQuery(id+"F0.wireOp",EDGE,"E25.0"),sQuery(id+"F0.wireOp",EDGE,"E25.1"),sQuery(id+"F0.wireOp",EDGE,"E25.2"),sQuery(id+"F0.wireOp",EDGE,"E25.3"),sQuery(id+"F0.wireOp",EDGE,"E25.4"),sQuery(id+"F0.wireOp",EDGE,"E25.5"),sQuery(id+"F0.wireOp",EDGE,"E25.6"),sQuery(id+"F0.wireOp",EDGE,"E25.7")])],"isStart":false});
            extrude(context, id + "F17", {"entities" : qUnion([Q0, Q1, Q2, Q3, Q4, Q5]), "endBound" : BoundingType.UP_TO_SURFACE, "endBoundEntityFace" : qUnion([Q6]), "depth" : 25 * mm});
        }
    });
